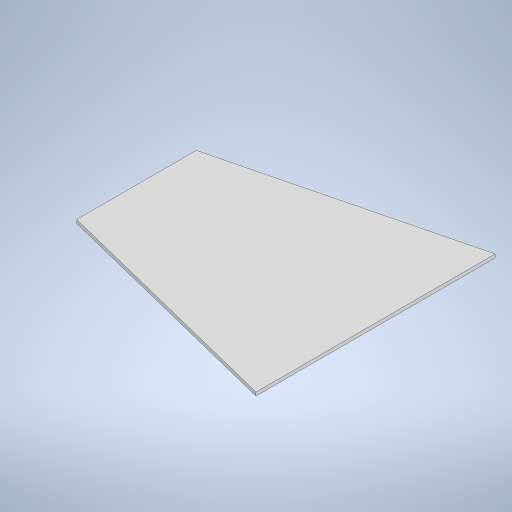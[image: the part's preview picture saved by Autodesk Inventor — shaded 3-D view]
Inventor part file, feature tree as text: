
AUTODESK INVENTOR PART (.ipt)
format: ipt  version: 2024.3 (Build 283343000, 343)  size: 213,504 bytes
history: native  units: mm
features: extrude x1, sketch x1
ambient origin geometry x8: Origin, YZ Plane, XZ Plane, XY Plane, X Axis, Y Axis, Z Axis, Center Point
bodies: Solid1 (feature_tree)
feature tree (2):
  extrude  "Extrusion1"  Depth=200.0mm
  sketch  "Sketch1"  dims[d0=200.0mm d1=200.0mm d2=50.0mm d3=50.0mm d4=0.0mm d5=3.0mm d6=0.0mm]
